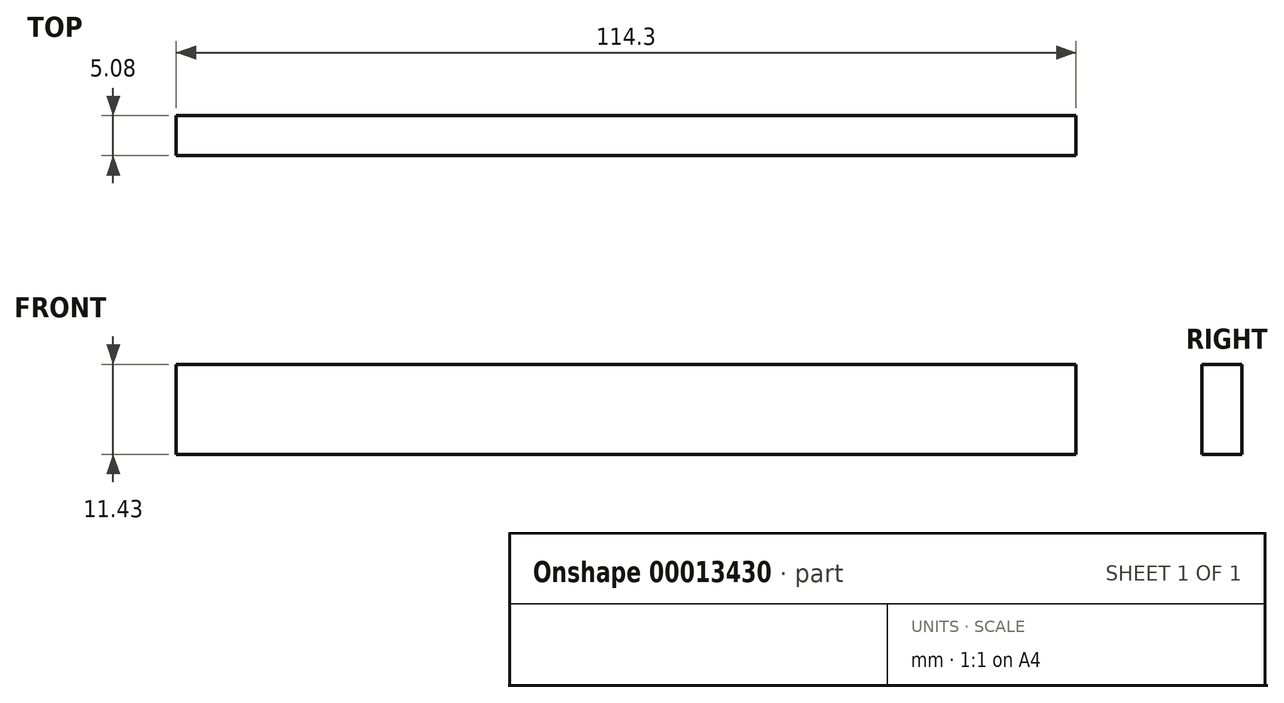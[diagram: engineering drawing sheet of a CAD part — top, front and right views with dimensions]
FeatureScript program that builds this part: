
annotation { "Feature Type Name" : "Feature", "Feature Type Description" : "" }
export const myFeature = defineFeature(function(context is Context, id is Id, definition is map)
    precondition{}
    {
        {
            var Q0;
            Q0=qCreatedBy(makeId("Front.planeOp"),FACE);
            var sketch = newSketch(context, id + "F0", { "sketchPlane" : qUnion([Q0])});
            skLineSegment(sketch, "E0.bottom", {"start": v(0, 0) * mm, "end": v(114.3, 0) * mm});
            skLineSegment(sketch, "E0.top", {"start": v(0, 11.43) * mm, "end": v(114.3, 11.43) * mm});
            skLineSegment(sketch, "E0.left", {"start": v(0, 0) * mm, "end": v(0, 11.43) * mm});
            skLineSegment(sketch, "E0.right", {"start": v(114.3, 0) * mm, "end": v(114.3, 11.43) * mm});
            skSolve(sketch);
        }
        {
            var Q0;
            Q0 = qSketchRegion(id + "F0", true);
            extrude(context, id + "F1", {"entities" : qUnion([Q0]), "depth" : 5.08 * mm});
        }
    });
